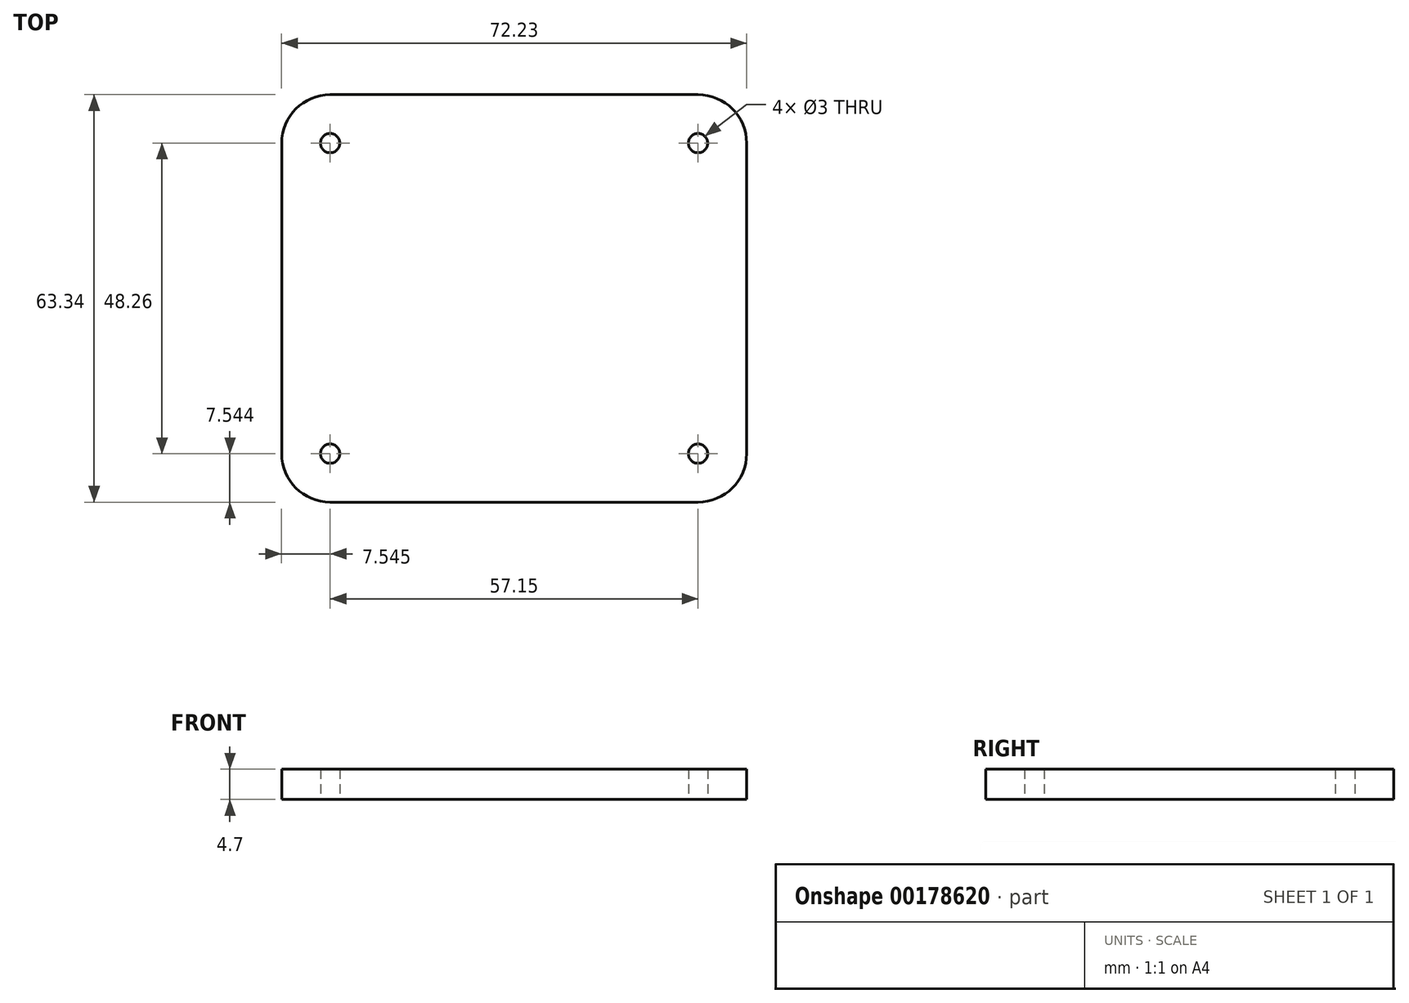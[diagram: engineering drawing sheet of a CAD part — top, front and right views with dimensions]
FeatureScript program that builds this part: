
annotation { "Feature Type Name" : "Feature", "Feature Type Description" : "" }
export const myFeature = defineFeature(function(context is Context, id is Id, definition is map)
    precondition{}
    {
        {
            var Q0;
            Q0=qCreatedBy(makeId("Top.planeOp"),FACE);
            var sketch = newSketch(context, id + "F0", { "sketchPlane" : qUnion([Q0])});
            skLineSegment(sketch, "E0.0", {"start": v(-38.8, 43.63) * mm, "end": v(18.35, 43.63) * mm});
            skArc(sketch, "E1.0", {"start": v(-46.34, 36.1) * mm, "mid": v(-44.13, 41.43) * mm, "end": v(-38.8, 43.63) * mm});
            skLineSegment(sketch, "E2.0", {"start": v(-46.34, -12.17) * mm, "end": v(-46.34, 36.1) * mm});
            skPoint(sketch, "E3.0", {"position": v(-44.13, -17.5) * mm});
            skArc(sketch, "E4.0", {"start": v(-38.8, -19.7) * mm, "mid": v(-44.13, -17.5) * mm, "end": v(-46.34, -12.17) * mm});
            skLineSegment(sketch, "E5.0", {"start": v(18.35, -19.7) * mm, "end": v(-38.8, -19.7) * mm});
            skArc(sketch, "E6.0", {"start": v(25.9, -12.17) * mm, "mid": v(23.69, -17.5) * mm, "end": v(18.35, -19.7) * mm});
            skLineSegment(sketch, "E7.0", {"start": v(25.9, 36.1) * mm, "end": v(25.9, -12.17) * mm});
            skArc(sketch, "E8.0", {"start": v(18.35, 43.63) * mm, "mid": v(23.69, 41.43) * mm, "end": v(25.9, 36.1) * mm});
            skCircle(sketch, "E9", {"center": v(-38.8, 36.1) * mm, "radius": 1.5 * mm});
            skCircle(sketch, "E10", {"center": v(18.35, 36.1) * mm, "radius": 1.5 * mm});
            skCircle(sketch, "E11", {"center": v(18.35, -12.17) * mm, "radius": 1.5 * mm});
            skCircle(sketch, "E12", {"center": v(-38.8, -12.17) * mm, "radius": 1.5 * mm});
            skSolve(sketch);
        }
        {
            var Q0;
            Q0 = qSketchRegion(id + "F0", true);
            extrude(context, id + "F1", {"entities" : qUnion([Q0]), "offsetDistance" : 25 * mm, "depth" : 4.7 * mm});
        }
    });
